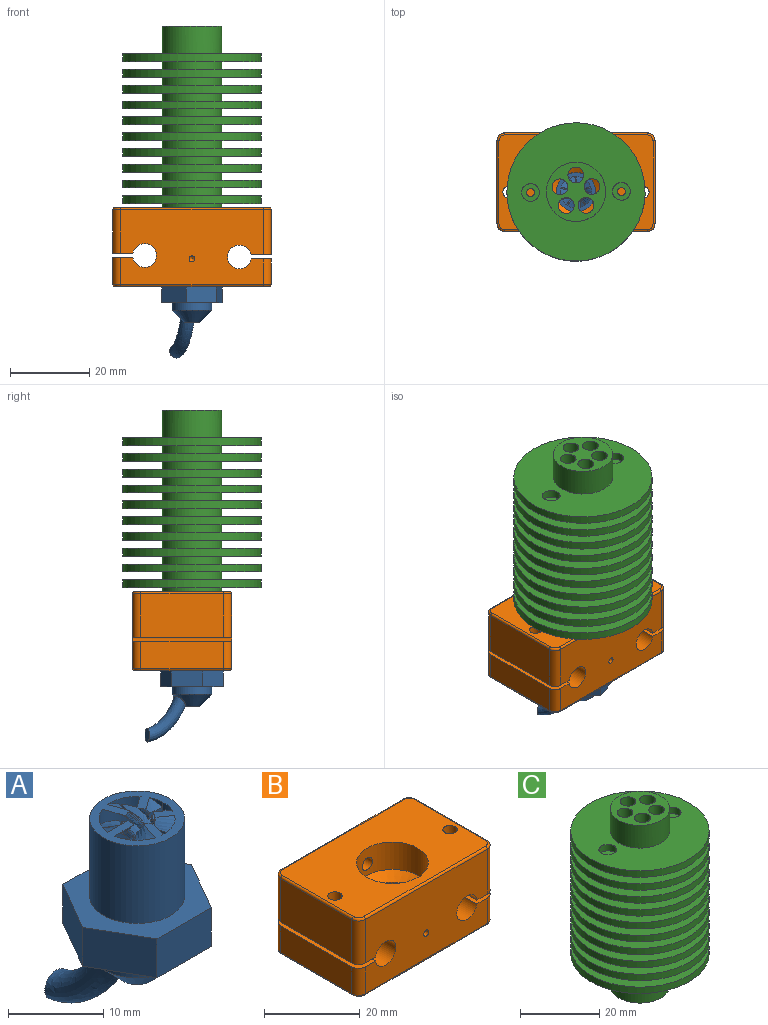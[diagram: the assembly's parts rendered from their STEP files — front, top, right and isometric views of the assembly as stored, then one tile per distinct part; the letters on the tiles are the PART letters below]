
ASSEMBLY  parts=3 mates=3
PART A: 214 faces, bbox 16.9x19.7x29.7 mm
  f0: cone r=3.3mm half-angle=57deg, axis (0,0,1), area 3.6mm2, adj f70,f101,f103,f158,f167
  f1: cone r=3.3mm half-angle=57deg, axis (0,0,1), area 3.6mm2, adj f31,f101,f103,f111,f132,f168
  f2: bspline ~7.35x3.98mm, area 9.2mm2, adj f4,f101,f199,f202
  f3: bspline ~3.2x3.15mm, area 4.9mm2, adj f5,f97,f101,f201
  f4: bspline ~2.5x2.07mm, area 0.5mm2, adj f2,f6,f199,f202
  f5: bspline ~1.23x1.07mm, area 0.3mm2, adj f3,f7,f97,f201
  f6: bspline ~2.5x2.14mm, area 0.4mm2, adj f4,f8,f199,f202
  f7: bspline ~2.5x1.59mm, area 0.3mm2, adj f5,f9,f97,f201
  f8: bspline ~2.5x2.19mm, area 0.3mm2, adj f6,f11,f199,f202
  f9: bspline ~2.5x1.8mm, area 0.3mm2, adj f7,f12,f97,f201
  f10: bspline ~2.52x2.5mm, area 0.9mm2, adj f113,f117,f119,f207,f208
  f11: bspline ~2.88x2.5mm, area 1.5mm2, adj f8,f14,f199,f202
  f12: bspline ~2.07x1.74mm, area 1.4mm2, adj f9,f15,f97,f201
  f13: bspline ~6.93x4.54mm, area 7.6mm2, adj f101,f118,f200,f203
  f14: bspline ~5.65x2.96mm, area 7.6mm2, adj f11,f101,f199,f202
  f15: bspline ~4.1x2.64mm, area 6.5mm2, adj f12,f97,f101,f201
  f16: bspline ~7.14x3.98mm, area 8mm2, adj f19,f101,f194,f195,f196
  f17: bspline ~5.61x3mm, area 8mm2, adj f20,f101,f192,f193
  f18: bspline ~2.98x2.78mm, area 3.8mm2, adj f21,f97,f101,f197
  f19: bspline ~3.75x3.51mm, area 0.5mm2, adj f16,f22,f194,f195
  f20: bspline ~3.75x3.51mm, area 0.5mm2, adj f17,f23,f192,f193
  f21: bspline ~1.43x1.25mm, area 0.3mm2, adj f18,f24,f97,f197
  f22: bspline ~3.75x3.6mm, area 0.4mm2, adj f19,f25,f194,f195
  f23: bspline ~3.75x3.6mm, area 0.4mm2, adj f20,f26,f192,f193
  f24: bspline ~1.29x1.25mm, area 0.3mm2, adj f21,f27,f97,f197
  f25: bspline ~2.99x2.5mm, area 1mm2, adj f22,f28,f194,f195,f196
  f26: bspline ~3.86x3.75mm, area 0.9mm2, adj f23,f29,f192,f193
  f27: bspline ~2.84x2.5mm, area 0.8mm2, adj f24,f30,f97,f197
  f28: bspline ~5.21x3.14mm, area 7.6mm2, adj f25,f101,f194,f196
  f29: bspline ~7.39x3.95mm, area 7.6mm2, adj f26,f101,f192,f193
  f30: bspline ~5.24x3.95mm, area 6mm2, adj f27,f97,f101,f197
  f31: plane 1.79x1.37mm, normal (0,0,-1), area 0.3mm2, adj f1,f45,f49,f190
  f32: bspline ~5.35x3.76mm, area 7.8mm2, adj f36,f101,f185,f186,f187
  f33: bspline ~7.38x3.76mm, area 7.7mm2, adj f37,f101,f184,f190
  f34: bspline ~3.06x2.57mm, area 2.2mm2, adj f38,f97,f102,f183
  f35: bspline ~6.09x5.61mm, area 7.8mm2, adj f39,f101,f182,f188
  f36: bspline ~2.71x2.5mm, area 0.5mm2, adj f32,f40,f185,f187
  f37: bspline ~3.75x3.73mm, area 0.5mm2, adj f33,f41,f184,f190
  f38: bspline ~1.75x1.25mm, area 0.1mm2, adj f34,f42,f97,f183
  f39: bspline ~3.75x3.13mm, area 0.5mm2, adj f35,f43,f182,f188
  f40: bspline ~2.72x2.5mm, area 0.4mm2, adj f36,f44,f185,f187
  f41: bspline ~3.75x3.6mm, area 0.4mm2, adj f37,f45,f184,f190
  f42: bspline ~1.66x1.25mm, area 0.1mm2, adj f38,f46,f97,f183
  f43: bspline ~3.75x3.05mm, area 0.4mm2, adj f39,f47,f182,f188
  f44: bspline ~3.75x3.4mm, area 0.9mm2, adj f40,f48,f185,f187
  f45: bspline ~3.75x3.55mm, area 0.9mm2, adj f31,f41,f49,f184,f190
  f46: bspline ~1.84x1.25mm, area 0.5mm2, adj f42,f50,f97,f183
  f47: bspline ~3.75x3.4mm, area 0.9mm2, adj f43,f131,f182,f188
  f48: bspline ~6.72x4.43mm, area 8mm2, adj f44,f101,f185,f186,f187
  f49: bspline ~5.64x2.78mm, area 7.6mm2, adj f31,f45,f101,f184
  f50: bspline ~2.91x2.78mm, area 4.8mm2, adj f46,f97,f101,f183
  f51: bspline ~3.75x2.52mm, area 0.4mm2, adj f54,f67,f170,f171
  f52: bspline ~0.54x0.48mm, area 0.1mm2, adj f55,f68,f132,f169
  f53: bspline ~2.5x1.59mm, area 0.5mm2, adj f56,f69,f97,f165
  f54: bspline ~3.75x2.62mm, area 0.8mm2, adj f51,f57,f170,f171
  f55: bspline ~1.25x1.18mm, area 0mm2, adj f52,f132,f169
  f56: bspline ~3.75x2.37mm, area 1.3mm2, adj f53,f58,f97,f165
  f57: bspline ~5.12x3.79mm, area 9.4mm2, adj f54,f101,f170,f171,f172,f173,f174
  f58: bspline ~6.02x5.69mm, area 14.7mm2, adj f56,f97,f101,f165,f176,f177,f178,f179
  f59: bspline ~3.22x2.93mm, area 1.5mm2, adj f97,f101,f181
  f60: bspline ~7.07x4.51mm, area 8.7mm2, adj f64,f101,f170,f172,f173,f174
  f61: bspline ~3.45x2.54mm, area 2.2mm2, adj f65,f101,f132,f169
  f62: bspline ~6.68x4.53mm, area 8.6mm2, adj f63,f101,f165,f178
  f63: bspline ~2.5x2.04mm, area 0.5mm2, adj f62,f69,f165,f176,f178
  f64: bspline ~2.5x2.37mm, area 0.5mm2, adj f60,f67,f170,f172
  f65: bspline ~1.29x1.25mm, area 0.2mm2, adj f61,f68,f132,f169
  f66: bspline ~1.25x1.14mm, area 0mm2, adj f97,f179,f180
  f67: bspline ~2.5x2.19mm, area 0.3mm2, adj f51,f64,f170,f171
  f68: bspline ~1.25x1.22mm, area 0.1mm2, adj f52,f65,f132,f169
  f69: bspline ~2.5x1.8mm, area 0.4mm2, adj f53,f63,f97,f165,f176,f177
  f70: plane 2.93x1.15mm, normal (0,0,-1), area 0.7mm2, adj f0,f71,f74,f160,f161,f162,f163
  f71: bspline ~3.17x2.93mm, area 1mm2, adj f70,f74,f101,f160,f161,f162,f163
  f72: bspline ~8.12x5mm, area 20.3mm2, adj f75,f101,f146,f149,f150,f151,f152,f153
  f73: bspline ~3.56x2.7mm, area 3.5mm2, adj f76,f97,f101,f147
  f74: bspline ~1.25x1mm, area 0mm2, adj f70,f71,f160
  f75: bspline ~5x2.12mm, area 1mm2, adj f72,f77,f146,f149
  f76: bspline ~1.25x0.86mm, area 0.1mm2, adj f73,f78,f97,f147
  f77: bspline ~5x2.05mm, area 0.8mm2, adj f75,f79,f146,f149
  f78: bspline ~1.25x0.88mm, area 0.2mm2, adj f76,f80,f97,f147
  f79: bspline ~5x2.24mm, area 1.4mm2, adj f77,f81,f146,f149
  f80: bspline ~2.5x1.48mm, area 0.5mm2, adj f78,f82,f97,f147
  f81: bspline ~5x2.62mm, area 0.8mm2, adj f79,f83,f146,f149
  f82: bspline ~1.57x1.22mm, area 0.4mm2, adj f80,f84,f97,f147
  f83: bspline ~7.43x6.57mm, area 19.4mm2, adj f81,f101,f146,f149,f150,f151,f152,f153
  f84: bspline ~4.56x3.6mm, area 7.3mm2, adj f82,f97,f101,f147
  f85: cone r=3.3mm half-angle=57deg, axis (0,0,1), area 3.6mm2, adj f101,f103,f107,f110,f120,f126
  f86: cone r=3.3mm half-angle=57deg, axis (0,0,1), area 3.6mm2, adj f101,f103,f139,f157,f210
  f87: cylinder r=0.88mm len=7.1mm, axis (0,0,-1), area 39.1mm2, adj f99,f103
  f88: plane 7x5mm, normal (-0.87,0.5,0), area 40.4mm2, adj f89,f93,f94,f95
  f89: plane 7x5mm, normal (-0.87,-0.5,0), area 40.4mm2, adj f88,f90,f94,f95
  f90: plane 8.08x5mm, normal (0,-1,0), area 40.4mm2, adj f89,f91,f94,f95
  f91: plane 7x5mm, normal (0.87,-0.5,0), area 40.4mm2, adj f90,f92,f94,f95
  f92: plane 7x5mm, normal (0.87,0.5,0), area 40.4mm2, adj f91,f93,f94,f95
  f93: plane 8.08x5mm, normal (0,1,0), area 40.4mm2, adj f88,f92,f94,f95
  f94: plane 16.17x14mm, normal (0,0,1), area 91.2mm2, adj f88,f89,f90,f91,f92,f93,f96
  f95: plane 16.17x14mm, normal (0,0,-1), area 91.2mm2, adj f88,f89,f90,f91,f92,f93,f98
  f96: cylinder r=5mm len=10mm, axis (0,0,-1), area 314.2mm2, adj f94,f97
  f97: plane 10x10mm, normal (0,0,1), area 40.6mm2, adj f3,f5,f7,f9,f12,f15,f18,f21
  f98: cylinder r=5mm len=10mm, axis (0,0,1), area 62.8mm2, adj f95,f100
  f99: plane 4.05x4.01mm, normal (0,0,-1), area 10.1mm2, adj f87,f100,f213
  f100: cone r=5mm half-angle=45deg, axis (0,0,1), area 83.6mm2, adj f98,f99,f212,f213
  f101: cylinder r=4mm len=8mm, axis (0,0,1), area 144.2mm2, adj f0,f1,f2,f3,f13,f14,f15,f16
  f102: cylinder r=4mm len=1.59mm, axis (0,0,1), area 0.5mm2, adj f34,f97,f101
  f103: cone r=0.75mm half-angle=24deg, axis (0,0,1), area 77mm2, adj f0,f1,f85,f86,f87,f104,f105,f106
  f104: cone r=3.3mm half-angle=57deg, axis (0,0,1), area 3.6mm2, adj f101,f103,f105,f108,f113
  f105: plane 1x0.95mm, normal (0,-1,0), area 0.6mm2, adj f101,f103,f104,f106
  f106: plane 0.95x0.34mm, normal (0,0,1), area 0.3mm2, adj f101,f103,f105,f210
  f107: plane 1x0.9mm, normal (0.95,-0.31,0), area 0.6mm2, adj f85,f101,f103,f109
  f108: plane 1x0.9mm, normal (-0.95,0.31,0), area 0.6mm2, adj f101,f103,f104,f109
  f109: plane 1.01x0.62mm, normal (0,0,1), area 0.3mm2, adj f101,f103,f107,f108
  f110: plane 1x0.77mm, normal (-0.59,-0.81,0), area 0.6mm2, adj f85,f101,f103,f112
  f111: plane 1x0.77mm, normal (0.59,0.81,0), area 0.6mm2, adj f1,f101,f103,f112
  f112: plane 0.97x0.83mm, normal (0,0,1), area 0.3mm2, adj f101,f103,f110,f111
  f113: plane 2.68x0.92mm, normal (0,0,-1), area 2.3mm2, adj f10,f104,f115,f116,f117,f119,f209
  f114: bspline ~8.14x5.46mm, area 19mm2, adj f101,f115,f200,f203,f204,f205,f206,f207
  f115: bspline ~5x2.8mm, area 1mm2, adj f113,f114,f116,f200,f209
  f116: bspline ~5x2.95mm, area 0.8mm2, adj f113,f115,f117,f200
  f117: bspline ~3.75x2.77mm, area 0.6mm2, adj f10,f113,f116,f118,f200,f206,f207
  f118: bspline ~2.88x2.5mm, area 1.5mm2, adj f13,f117,f200,f203,f204,f205
  f119: bspline ~4.54x4.15mm, area 5.3mm2, adj f10,f101,f113,f208
  f120: plane 2.15x1.36mm, normal (0,0,-1), area 1.5mm2, adj f85,f122,f123,f124,f125,f198
  f121: bspline ~5.61x3mm, area 8mm2, adj f101,f122,f191,f198
  f122: bspline ~2.82x2.5mm, area 0.5mm2, adj f120,f121,f123,f191,f198
  f123: bspline ~2x1.71mm, area 0.4mm2, adj f120,f122,f124,f191
  f124: bspline ~2.84x2.5mm, area 0.7mm2, adj f120,f123,f125,f191
  f125: bspline ~5.24x3.95mm, area 5.8mm2, adj f101,f120,f124,f191
  f126: plane 2.02x1.63mm, normal (0,0,-1), area 1.1mm2, adj f85,f127,f128,f129,f130,f189
  f127: bspline ~3.23x2.62mm, area 1.3mm2, adj f101,f126,f128,f189
  f128: bspline ~0.61x0.49mm, area 0.1mm2, adj f126,f127,f129,f189
  f129: bspline ~1.29x1.25mm, area 0mm2, adj f126,f128,f130,f189
  f130: bspline ~0.02x0.01mm, area 0mm2, adj f126,f129,f189
  f131: bspline ~6.72x4.43mm, area 8mm2, adj f47,f101,f182,f188
  f132: plane 2.5x2.05mm, normal (0,0,-1), area 1.8mm2, adj f1,f52,f55,f61,f65,f68,f169
  f133: bspline ~2.5x1.59mm, area 0.4mm2, adj f134,f138,f164,f175
  f134: bspline ~2.5x1.91mm, area 0.8mm2, adj f133,f135,f164,f175
  f135: bspline ~5.12x3.79mm, area 9.2mm2, adj f101,f134,f164,f175
  f136: bspline ~7.07x4.51mm, area 8.6mm2, adj f101,f137,f164,f175
  f137: bspline ~3.75x2.75mm, area 0.4mm2, adj f136,f138,f164,f175
  f138: bspline ~3.75x2.54mm, area 0.3mm2, adj f133,f137,f164,f175
  f139: plane 2.98x1.34mm, normal (0,0,-1), area 1.3mm2, adj f86,f143,f144,f145,f159
  f140: bspline ~6.68x4.53mm, area 9.6mm2, adj f101,f141,f148,f159
  f141: bspline ~3.75x1.76mm, area 0.4mm2, adj f140,f142,f148,f159
  f142: bspline ~2.5x1.14mm, area 0.3mm2, adj f141,f143,f148,f159
  f143: bspline ~2.5x1.48mm, area 0.5mm2, adj f139,f142,f144,f148,f159
  f144: bspline ~2.5x1.74mm, area 0.2mm2, adj f139,f143,f145,f148
  f145: bspline ~4.56x3.6mm, area 7.5mm2, adj f101,f139,f144,f148
  f146: plane 2.48x1.81mm, normal (-0.59,-0.81,0), area 2.2mm2, adj f72,f75,f77,f79,f81,f83,f101
  f147: plane 2.84x2.18mm, normal (0.59,0.81,0), area 2.2mm2, adj f73,f76,f78,f80,f82,f84,f101
  f148: plane 3.7x2.02mm, normal (0,1,0), area 2.2mm2, adj f101,f140,f141,f142,f143,f144,f145
  f149: plane 3.06x1.47mm, normal (0,-1,0), area 2.2mm2, adj f72,f75,f77,f79,f81,f83,f101
  f150: plane 2.27x1.01mm, normal (-0.95,0.31,0), area 1.5mm2, adj f72,f83,f101,f151
  f151: cylinder r=1.49mm len=1.38mm, axis (0,0,1), area 0.4mm2, adj f72,f83,f150,f152
  f152: plane 1.09x0.02mm, normal (0.95,-0.31,0), area 0mm2, adj f72,f83,f151,f153
  f153: plane 1.14x0.11mm, normal (0.31,-0.95,0), area 0.1mm2, adj f72,f83,f152,f154
  f154: plane 1.08x0.15mm, normal (0.95,0.31,0), area 0.2mm2, adj f72,f83,f153,f155
  f155: plane 2.18x0.95mm, normal (0.95,-0.31,0), area 1.4mm2, adj f72,f83,f101,f154
  f156: plane 1.01x0.62mm, normal (0,0,1), area 0.3mm2, adj f101,f103,f157,f158
  f157: plane 1x0.9mm, normal (-0.95,-0.31,0), area 0.6mm2, adj f86,f101,f103,f156
  f158: plane 1x0.9mm, normal (0.95,0.31,0), area 0.6mm2, adj f0,f101,f103,f156
  f159: plane 3.58x1.63mm, normal (-0.95,-0.31,0), area 1.3mm2, adj f101,f139,f140,f141,f142,f143
  f160: plane 0.54x0.38mm, normal (0.95,0.31,0), area 0.1mm2, adj f70,f71,f74,f163
  f161: plane 1.88x0.65mm, normal (0.95,0.31,0), area 0.2mm2, adj f70,f71,f101,f162
  f162: plane 0.5x0.48mm, normal (0.95,-0.31,0), area 0.1mm2, adj f70,f71,f161,f163
  f163: plane 0.48x0.34mm, normal (0.31,0.95,0), area 0.1mm2, adj f70,f71,f160,f162
  f164: plane 3.02x1.39mm, normal (0,1,0), area 1.7mm2, adj f101,f133,f134,f135,f136,f137,f138
  f165: plane 3.14x1.44mm, normal (0,-1,0), area 1.7mm2, adj f53,f56,f58,f62,f63,f69,f101
  f166: plane 0.97x0.83mm, normal (0,0,1), area 0.3mm2, adj f101,f103,f167,f168
  f167: plane 1x0.77mm, normal (-0.59,0.81,0), area 0.6mm2, adj f0,f101,f103,f166
  f168: plane 1x0.77mm, normal (0.59,-0.81,0), area 0.6mm2, adj f1,f101,f103,f166
  f169: plane 2.5x1.91mm, normal (0.59,-0.81,0), area 1.2mm2, adj f52,f55,f61,f65,f68,f101,f132
  f170: plane 2.2x1.6mm, normal (-0.59,0.81,0), area 1.7mm2, adj f51,f54,f57,f60,f64,f67,f101
  f171: plane 1.02x0.2mm, normal (0.95,0.31,0), area 0.1mm2, adj f51,f54,f57,f67,f172
  f172: plane 1.27x0.34mm, normal (0.31,0.95,0), area 0.3mm2, adj f57,f60,f64,f171,f174
  f173: plane 1.89x0.85mm, normal (0.95,0.31,0), area 1mm2, adj f57,f60,f101,f174
  f174: plane 1.2x0.47mm, normal (0.95,-0.31,0), area 0.4mm2, adj f57,f60,f172,f173
  f175: plane 3.03x1.47mm, normal (-0.95,-0.31,0), area 1.7mm2, adj f101,f133,f134,f135,f136,f137,f138
  f176: cylinder r=1.49mm len=1.26mm, axis (0,0,1), area 0.3mm2, adj f58,f63,f69,f177,f178
  f177: plane 0.97x0.02mm, normal (0.95,-0.31,0), area 0mm2, adj f58,f69,f176,f179
  f178: plane 2.61x1.33mm, normal (-0.95,0.31,0), area 1.5mm2, adj f58,f62,f63,f101,f176
  f179: plane 1.06x0.11mm, normal (0.31,-0.95,0), area 0.1mm2, adj f58,f66,f177,f180
  f180: plane 1.07x0.15mm, normal (0.95,0.31,0), area 0.1mm2, adj f58,f66,f179,f181
  f181: plane 2.67x1.48mm, normal (0.95,-0.31,0), area 1.4mm2, adj f58,f59,f101,f180
  f182: plane 2.27x0.98mm, normal (0,1,0), area 1.2mm2, adj f35,f39,f43,f47,f101,f131
  f183: plane 2.37x1.07mm, normal (0,-1,0), area 1.2mm2, adj f34,f38,f42,f46,f50,f101
  f184: plane 1.87x1.4mm, normal (0.59,-0.81,0), area 1.2mm2, adj f33,f37,f41,f45,f49,f101
  f185: plane 1.76x1.29mm, normal (-0.59,0.81,0), area 1.2mm2, adj f32,f36,f40,f44,f48,f101
  f186: plane 1.94x0.9mm, normal (0.95,0.31,0), area 1.1mm2, adj f32,f48,f101,f187
  f187: plane 0.86x0.25mm, normal (0.95,-0.31,0), area 0.2mm2, adj f32,f36,f40,f44,f48,f186
  f188: plane 2.26x1.05mm, normal (-0.95,-0.31,0), area 1.2mm2, adj f35,f39,f43,f47,f101,f131
  f189: plane 1.86x1.39mm, normal (-0.59,-0.81,0), area 0.6mm2, adj f101,f126,f127,f128,f129,f130
  f190: plane 1.96x1.49mm, normal (0.59,0.81,0), area 1mm2, adj f31,f33,f37,f41,f45,f101
  f191: plane 1.99x1.52mm, normal (-0.59,-0.81,0), area 1.2mm2, adj f101,f121,f122,f123,f124,f125
  f192: plane 1.91x1.44mm, normal (0.59,0.81,0), area 1.1mm2, adj f17,f20,f23,f26,f29,f101
  f193: plane 2x1.53mm, normal (0.59,-0.81,0), area 1.2mm2, adj f17,f20,f23,f26,f29,f101
  f194: plane 1.91x1.45mm, normal (-0.59,0.81,0), area 1.2mm2, adj f16,f19,f22,f25,f28,f101
  f195: plane 0.9x0.24mm, normal (0.95,-0.31,0), area 0.1mm2, adj f16,f19,f22,f25,f196
  f196: plane 2.09x1.08mm, normal (0.95,0.31,0), area 1mm2, adj f16,f25,f28,f101,f195
  f197: plane 2.21x0.99mm, normal (-0.95,-0.31,0), area 1.1mm2, adj f18,f21,f24,f27,f30,f101
  f198: plane 2.1x0.74mm, normal (0.95,-0.31,0), area 0.3mm2, adj f101,f120,f121,f122
  f199: plane 2.43x1.84mm, normal (0.59,0.81,0), area 1.6mm2, adj f2,f4,f6,f8,f11,f14,f101
  f200: plane 2.5x1.9mm, normal (-0.59,-0.81,0), area 1.6mm2, adj f13,f101,f114,f115,f116,f117,f118
  f201: plane 2.42x1.83mm, normal (-0.59,0.81,0), area 1.6mm2, adj f3,f5,f7,f9,f12,f15,f101
  f202: plane 2.5x1.9mm, normal (0.59,-0.81,0), area 1.6mm2, adj f2,f4,f6,f8,f11,f14,f101
  f203: plane 2.44x1.07mm, normal (0.95,-0.31,0), area 1.4mm2, adj f13,f101,f114,f118,f204
  f204: plane 0.83x0.15mm, normal (0.95,0.31,0), area 0.1mm2, adj f114,f118,f203,f205
  f205: plane 0.84x0.11mm, normal (0.31,-0.95,0), area 0.1mm2, adj f114,f118,f204,f206
  f206: plane 0.73x0.02mm, normal (0.95,-0.31,0), area 0mm2, adj f114,f117,f205,f207
  f207: cylinder r=1.49mm len=1.09mm, axis (0,0,1), area 0.3mm2, adj f10,f114,f117,f206,f208
  f208: plane 2.61x1.25mm, normal (-0.95,0.31,0), area 1.5mm2, adj f10,f101,f114,f119,f207
  f209: plane 2.68x0.1mm, normal (0,-1,0), area 0.1mm2, adj f101,f113,f114,f115
  f210: plane 1x0.95mm, normal (0,1,0), area 0.6mm2, adj f86,f101,f103,f106
  f211: plane 3.99x3.99mm, normal (0,1,0), area 9.6mm2, adj f213
  f212: plane 3.29x1.13mm, normal (0,-0.38,0.92), area 0.6mm2, adj f100,f213
  f213: bspline ~11.6x10.49mm, area 141.2mm2, adj f99,f100,f211,f212
PART B: 51 faces, bbox 40.3x25.3x20 mm
  f0: cylinder r=7.5mm len=15mm, axis (0,0,1), area 322.8mm2, adj f10,f46,f50
  f1: cylinder r=5mm len=11.5mm, axis (0,0,-1), area 355.3mm2, adj f11,f46,f47,f48
  f2: plane 21x6.87mm, normal (-1,0,0), area 144.3mm2, adj f15,f22,f23,f38
  f3: plane 36x19mm, normal (0,1,0), area 607.3mm2, adj f4,f6,f12,f13,f14,f15,f22,f24
  f4: cylinder r=3mm len=25mm, axis (0,-1,0), area 446.1mm2, adj f3,f9,f14,f15
  f5: plane 21x6.5mm, normal (1,0,0), area 136.5mm2, adj f12,f24,f25,f45
  f6: cylinder r=3mm len=25mm, axis (0,-1,0), area 446.1mm2, adj f3,f9,f12,f13
  f7: plane 21x11.5mm, normal (1,0,0), area 241.5mm2, adj f13,f26,f29,f37
  f8: plane 21x11.13mm, normal (-1,0,0), area 233.7mm2, adj f14,f27,f28,f30
  f9: plane 36x19mm, normal (0,-1,0), area 619.7mm2, adj f4,f6,f12,f13,f14,f15,f21,f23
  f10: plane 39x24mm, normal (0,0,1), area 743.2mm2, adj f0,f17,f18,f30,f31,f32,f33,f34
  f11: plane 39x24mm, normal (0,0,-1), area 841.4mm2, adj f1,f16,f19,f38,f39,f40,f41,f42
  f12: plane 25x5.04mm, normal (0,0,1), area 117.3mm2, adj f3,f5,f6,f9,f19,f24,f25
  f13: plane 25x5.04mm, normal (0,0,-1), area 117.3mm2, adj f3,f6,f7,f9,f18,f26,f29
  f14: plane 25x5.04mm, normal (0,0,-1), area 117.3mm2, adj f3,f4,f8,f9,f17,f27,f28
  f15: plane 25x5.04mm, normal (0,0,1), area 117.3mm2, adj f2,f3,f4,f9,f16,f22,f23
  f16: cylinder r=1.5mm len=7.37mm, axis (0,0,-1), area 69.5mm2, adj f11,f15
  f17: cylinder r=1.5mm len=11.63mm, axis (0,0,-1), area 109.6mm2, adj f10,f14
  f18: cylinder r=1.5mm len=12mm, axis (0,0,-1), area 113.1mm2, adj f10,f13
  f19: cylinder r=1.5mm len=7mm, axis (0,0,-1), area 66mm2, adj f11,f12
  f20: cone r=0mm half-angle=59deg, axis (0,-1,0), area 2.1mm2, adj f21
  f21: cylinder r=0.75mm len=3mm, axis (0,-1,0), area 14.1mm2, adj f9,f20
  f22: cylinder r=2mm len=6.87mm, axis (0,0,-1), area 21.6mm2, adj f2,f3,f15,f39
  f23: cylinder r=2mm len=6.87mm, axis (0,0,1), area 21.6mm2, adj f2,f9,f15,f40
  f24: cylinder r=2mm len=6.5mm, axis (0,0,1), area 20.4mm2, adj f3,f5,f12,f43
  f25: cylinder r=2mm len=6.5mm, axis (0,0,-1), area 20.4mm2, adj f5,f9,f12,f44
  f26: cylinder r=2mm len=11.5mm, axis (0,0,1), area 36.1mm2, adj f3,f7,f13,f35
  f27: cylinder r=2mm len=11.13mm, axis (0,0,-1), area 35mm2, adj f3,f8,f14,f31
  f28: cylinder r=2mm len=11.13mm, axis (0,0,1), area 35mm2, adj f8,f9,f14,f32
  f29: cylinder r=2mm len=11.5mm, axis (0,0,-1), area 36.1mm2, adj f7,f9,f13,f36
  f30: cylinder r=0.5mm len=21mm, axis (0,1,0), area 16.5mm2, adj f8,f10,f31,f32
  f31: torus R=1.5mm, axis (0,0,1), area 2.2mm2, adj f10,f27,f30,f33
  f32: torus R=1.5mm, axis (0,0,1), area 2.2mm2, adj f10,f28,f30,f34
  f33: cylinder r=0.5mm len=36mm, axis (1,0,0), area 28.3mm2, adj f3,f10,f31,f35
  f34: cylinder r=0.5mm len=36mm, axis (-1,0,0), area 28.3mm2, adj f9,f10,f32,f36
  f35: torus R=1.5mm, axis (0,0,1), area 2.2mm2, adj f10,f26,f33,f37
  f36: torus R=1.5mm, axis (0,0,1), area 2.2mm2, adj f10,f29,f34,f37
  f37: cylinder r=0.5mm len=21mm, axis (0,-1,0), area 16.5mm2, adj f7,f10,f35,f36
  f38: cylinder r=0.5mm len=21mm, axis (0,-1,0), area 16.5mm2, adj f2,f11,f39,f40
  f39: torus R=1.5mm, axis (0,0,1), area 2.2mm2, adj f11,f22,f38,f41
  f40: torus R=1.5mm, axis (0,0,1), area 2.2mm2, adj f11,f23,f38,f42
  f41: cylinder r=0.5mm len=36mm, axis (-1,0,0), area 28.3mm2, adj f3,f11,f39,f43
  f42: cylinder r=0.5mm len=36mm, axis (1,0,0), area 28.3mm2, adj f9,f11,f40,f44
  f43: torus R=1.5mm, axis (0,0,1), area 2.2mm2, adj f11,f24,f41,f45
  f44: torus R=1.5mm, axis (0,0,1), area 2.2mm2, adj f11,f25,f42,f45
  f45: cylinder r=0.5mm len=21mm, axis (0,1,0), area 16.5mm2, adj f5,f11,f43,f44
  f46: cone r=0mm half-angle=59deg, axis (0,0,1), area 114.5mm2, adj f0,f1
  f47: cone r=0mm half-angle=59deg, axis (0,1,0), area 0.7mm2, adj f1,f49
  f48: cone r=0mm half-angle=59deg, axis (0,1,0), area 0.7mm2, adj f1,f49
  f49: cylinder r=1.5mm len=10mm, axis (0,1,0), area 94.2mm2, adj f3,f47,f48
  f50: cylinder r=1.5mm len=7.65mm, axis (0,1,0), area 71.4mm2, adj f0,f3
PART C: 68 faces, bbox 35x35x55 mm
  f0: cylinder r=7.5mm len=15mm, axis (0,0,-1), area 329.9mm2, adj f16,f44
  f1: cylinder r=7.5mm len=15mm, axis (0,0,-1), area 94.2mm2, adj f41,f45
  f2: cylinder r=7.5mm len=15mm, axis (0,0,-1), area 94.2mm2, adj f38,f42
  f3: cylinder r=7.5mm len=15mm, axis (0,0,-1), area 94.2mm2, adj f35,f39
  f4: cylinder r=7.5mm len=15mm, axis (0,0,-1), area 94.2mm2, adj f32,f36
  f5: cylinder r=7.5mm len=15mm, axis (0,0,-1), area 94.2mm2, adj f29,f33
  f6: cylinder r=7.5mm len=15mm, axis (0,0,-1), area 94.2mm2, adj f26,f30
  f7: cylinder r=7.5mm len=15mm, axis (0,0,-1), area 94.2mm2, adj f23,f27
  f8: cylinder r=7.5mm len=15mm, axis (0,0,-1), area 94.2mm2, adj f20,f24
  f9: cylinder r=7.5mm len=15mm, axis (0,0,-1), area 94.2mm2, adj f19,f21
  f10: cylinder r=2mm len=55mm, axis (0,0,-1), area 691.2mm2, adj f16,f47
  f11: cylinder r=2mm len=55mm, axis (0,0,-1), area 691.2mm2, adj f16,f47
  f12: cylinder r=2mm len=55mm, axis (0,0,-1), area 691.2mm2, adj f16,f47
  f13: cylinder r=2mm len=55mm, axis (0,0,-1), area 691.2mm2, adj f16,f47
  f14: cylinder r=2mm len=55mm, axis (0,0,-1), area 691.2mm2, adj f16,f47
  f15: cylinder r=7.5mm len=15mm, axis (0,0,-1), area 471.2mm2, adj f17,f47
  f16: plane 15x15mm, normal (0,0,1), area 113.9mm2, adj f0,f10,f11,f12,f13,f14
  f17: plane 35x35mm, normal (0,0,-1), area 779.1mm2, adj f15,f18,f54,f55
  f18: cylinder r=17.5mm len=35mm, axis (0,0,-1), area 219.9mm2, adj f17,f19
  f19: plane 35x35mm, normal (0,0,1), area 779.1mm2, adj f9,f18,f54,f55
  f20: plane 35x35mm, normal (0,0,1), area 779.1mm2, adj f8,f22,f52,f53
  f21: plane 35x35mm, normal (0,0,-1), area 779.1mm2, adj f9,f22,f52,f53
  f22: cylinder r=17.5mm len=35mm, axis (0,0,-1), area 219.9mm2, adj f20,f21
  f23: plane 35x35mm, normal (0,0,1), area 779.1mm2, adj f7,f25,f50,f51
  f24: plane 35x35mm, normal (0,0,-1), area 779.1mm2, adj f8,f25,f50,f51
  f25: cylinder r=17.5mm len=35mm, axis (0,0,-1), area 219.9mm2, adj f23,f24
  f26: plane 35x35mm, normal (0,0,1), area 779.1mm2, adj f6,f28,f48,f49
  f27: plane 35x35mm, normal (0,0,-1), area 779.1mm2, adj f7,f28,f48,f49
  f28: cylinder r=17.5mm len=35mm, axis (0,0,-1), area 219.9mm2, adj f26,f27
  f29: plane 35x35mm, normal (0,0,1), area 753.6mm2, adj f5,f31,f66,f67
  f30: plane 35x35mm, normal (0,0,-1), area 753.6mm2, adj f6,f31,f66,f67
  f31: cylinder r=17.5mm len=35mm, axis (0,0,-1), area 219.9mm2, adj f29,f30
  f32: plane 35x35mm, normal (0,0,1), area 753.6mm2, adj f4,f34,f64,f65
  f33: plane 35x35mm, normal (0,0,-1), area 753.6mm2, adj f5,f34,f64,f65
  f34: cylinder r=17.5mm len=35mm, axis (0,0,-1), area 219.9mm2, adj f32,f33
  f35: plane 35x35mm, normal (0,0,1), area 753.6mm2, adj f3,f37,f62,f63
  f36: plane 35x35mm, normal (0,0,-1), area 753.6mm2, adj f4,f37,f62,f63
  f37: cylinder r=17.5mm len=35mm, axis (0,0,-1), area 219.9mm2, adj f35,f36
  f38: plane 35x35mm, normal (0,0,1), area 753.6mm2, adj f2,f40,f60,f61
  f39: plane 35x35mm, normal (0,0,-1), area 753.6mm2, adj f3,f40,f60,f61
  f40: cylinder r=17.5mm len=35mm, axis (0,0,-1), area 219.9mm2, adj f38,f39
  f41: plane 35x35mm, normal (0,0,1), area 753.6mm2, adj f1,f43,f58,f59
  f42: plane 35x35mm, normal (0,0,-1), area 753.6mm2, adj f2,f43,f58,f59
  f43: cylinder r=17.5mm len=35mm, axis (0,0,-1), area 219.9mm2, adj f41,f42
  f44: plane 35x35mm, normal (0,0,1), area 753.6mm2, adj f0,f46,f56,f57
  f45: plane 35x35mm, normal (0,0,-1), area 753.6mm2, adj f1,f46,f56,f57
  f46: cylinder r=17.5mm len=35mm, axis (0,0,-1), area 219.9mm2, adj f44,f45
  f47: plane 15x15mm, normal (0,0,-1), area 113.9mm2, adj f10,f11,f12,f13,f14,f15
  f48: cylinder r=1mm len=2mm, axis (0,0,1), area 12.6mm2, adj f26,f27
  f49: cylinder r=1mm len=2mm, axis (0,0,1), area 12.6mm2, adj f26,f27
  f50: cylinder r=1mm len=2mm, axis (0,0,1), area 12.6mm2, adj f23,f24
  f51: cylinder r=1mm len=2mm, axis (0,0,1), area 12.6mm2, adj f23,f24
  f52: cylinder r=1mm len=2mm, axis (0,0,1), area 12.6mm2, adj f20,f21
  f53: cylinder r=1mm len=2mm, axis (0,0,1), area 12.6mm2, adj f20,f21
  f54: cylinder r=1mm len=2mm, axis (0,0,1), area 12.6mm2, adj f17,f19
  f55: cylinder r=1mm len=2mm, axis (0,0,1), area 12.6mm2, adj f17,f19
  f56: cylinder r=2.25mm len=4.5mm, axis (0,0,1), area 28.3mm2, adj f44,f45
  f57: cylinder r=2.25mm len=4.5mm, axis (0,0,1), area 28.3mm2, adj f44,f45
  f58: cylinder r=2.25mm len=4.5mm, axis (0,0,1), area 28.3mm2, adj f41,f42
  f59: cylinder r=2.25mm len=4.5mm, axis (0,0,1), area 28.3mm2, adj f41,f42
  f60: cylinder r=2.25mm len=4.5mm, axis (0,0,1), area 28.3mm2, adj f38,f39
  f61: cylinder r=2.25mm len=4.5mm, axis (0,0,1), area 28.3mm2, adj f38,f39
  f62: cylinder r=2.25mm len=4.5mm, axis (0,0,1), area 28.3mm2, adj f35,f36
  f63: cylinder r=2.25mm len=4.5mm, axis (0,0,1), area 28.3mm2, adj f35,f36
  f64: cylinder r=2.25mm len=4.5mm, axis (0,0,1), area 28.3mm2, adj f32,f33
  f65: cylinder r=2.25mm len=4.5mm, axis (0,0,1), area 28.3mm2, adj f32,f33
  f66: cylinder r=2.25mm len=4.5mm, axis (0,0,1), area 28.3mm2, adj f29,f30
  f67: cylinder r=2.25mm len=4.5mm, axis (0,0,1), area 28.3mm2, adj f29,f30
PLACE A rot(axis=(0,0,1),19.3deg) t=(16.3,6.56,-9.56)mm
PLACE B t=(16.3,6.56,-5.52)mm fixed
PLACE C rot(axis=(0,0,1),0.7deg) t=(16.3,6.56,10.44)mm
MATE planar C.f0 <-> A.f97  axis (0,0,-1) through (16.3,6.56,5.44)mm
MATE cylindrical A.f0 <-> B.f11  axis (0,0,1) through (16.3,6.56,-4.56)mm
MATE cylindrical B.f0 <-> A.f0  axis (0,0,-1) through (16.3,6.56,-5.52)mm
